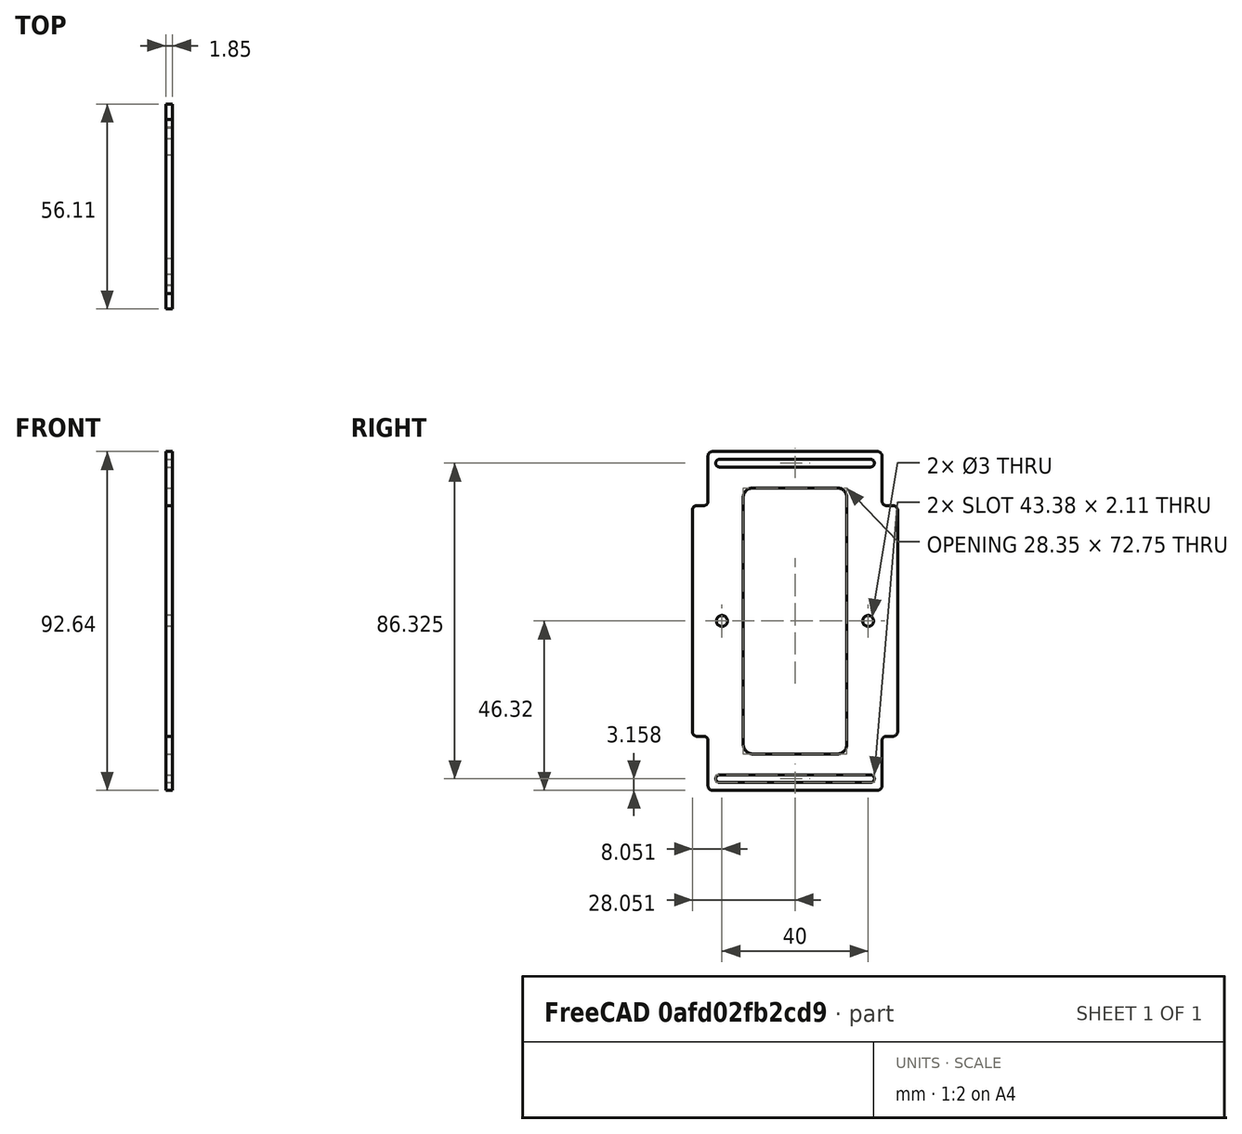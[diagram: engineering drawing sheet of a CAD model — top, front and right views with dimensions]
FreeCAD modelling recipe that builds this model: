
FCSTD DOCUMENT  (FreeCAD 1.0R38641 +468 (Git))
Label: psu_side_short
License: All rights reserved
LicenseURL: https://en.wikipedia.org/wiki/All_rights_reserved
objects: PartDesign::SubShapeBinder×2, Sketcher::SketchObject×1, PartDesign::Pad×1, PartDesign::Body×1
note: 8 computed .brp shape members not serialized (recipe doc carries the construction recipe); baked Part::Feature solids carry a one-line shape summary decoded from their .brp
EXTERNAL_REF file=../../third_party/qualtek_power_entry.FCStd obj=Body
EXTERNAL_REF file=psu_top_and_bottom.FCStd obj=Body
EXTERNAL_REF file=../dimensions.FCStd obj=VarSet

FEATURE [PartDesign::SubShapeBinder] Binder  label="PowerEntryBinder"
  BindCopyOnChange = 0
  BindMode = 0
  ClaimChildren = false
  Context = -> Body [Binder.]
  Fuse = false
  MakeFace = true
  OffsetFill = false
  OffsetIntersection = false
  OffsetJoinType = 0
  OffsetOpenResult = false
  PartialLoad = false
  Placement = pos=(0,0,0) rot=(1,0,0;1.5708rad)
  Refine = true
  Relative = true
  Support = -> [<external ../../third_party/qualtek_power_entry.FCStd>#Body]
  _Version = 2
FEATURE [PartDesign::SubShapeBinder] Binder001  label="PsuTopAndBottomBinder"
  BindCopyOnChange = 0
  BindMode = 0
  ClaimChildren = false
  Context = -> Body [Binder001.]
  Fuse = false
  MakeFace = true
  OffsetFill = false
  OffsetIntersection = false
  OffsetJoinType = 0
  OffsetOpenResult = false
  PartialLoad = false
  Refine = true
  Relative = true
  Support = -> [<external psu_top_and_bottom.FCStd>#Body]
  _Version = 2
FEATURE [Sketcher::SketchObject] Sketch
  ArcFitTolerance = 1e-06
  AttachmentSupport = -> [Binder001]
  ExternalGeometry = -> [Binder001,Binder]
  FullyConstrained = true
  MakeInternals = false
  MapMode = 5
  Placement = pos=(326.108,0,0) rot=(0.57735,0.57735,0.57735;2.0944rad)
  expr: Constraints[141] = dimensions#VarSet.EnclosureFinishThickness
  expr: Constraints[165] = dimensions#VarSet.EnclosureTotalThickness + 2 * dimensions#VarSet.EnclosureFinishThickness
  expr: Constraints[2] = dimensions#VarSet.EnclosureFinishThickness
  expr: Constraints[31] = dimensions#VarSet.EnclosureCornerRadius
  expr: Constraints[3] = dimensions#VarSet.EnclosureFinishThickness
  sketch-geometry (76):
    g0: LineSegment [constr] StartX=129.081 StartY=-24.706 StartZ=0 EndX=129.081 EndY=-87.794 EndZ=0
    g1: LineSegment StartX=129.081 StartY=-24.706 StartZ=0 EndX=127.227 EndY=-24.706 EndZ=0
    g2: LineSegment StartX=129.081 StartY=-87.794 StartZ=0 EndX=127.227 EndY=-87.794 EndZ=0
    g3: LineSegment StartX=126.027 StartY=-86.594 StartZ=0 EndX=126.027 EndY=-25.906 EndZ=0
    g4: ArcOfCircle CenterX=129.081 CenterY=-88.994 CenterZ=0 NormalX=0 NormalY=0 NormalZ=1 AngleXU=0 Radius=1.2 StartAngle=-2.7e-15 EndAngle=1.5708
    g5: ArcOfCircle CenterX=129.081 CenterY=-23.506 CenterZ=0 NormalX=0 NormalY=0 NormalZ=1 AngleXU=0 Radius=1.2 StartAngle=4.71239 EndAngle=6.28319
    g6: LineSegment StartX=130.281 StartY=-11.1254 StartZ=0 EndX=130.281 EndY=-23.506 EndZ=0
    g7: LineSegment StartX=130.281 StartY=-88.994 StartZ=0 EndX=130.281 EndY=-101.375 EndZ=0
    g8: LineSegment StartX=131.481 StartY=-102.575 StartZ=0 EndX=176.681 EndY=-102.575 EndZ=0
    g9: LineSegment StartX=131.481 StartY=-9.9254 StartZ=0 EndX=176.681 EndY=-9.9254 EndZ=0
    g10: LineSegment StartX=177.881 StartY=-11.1254 StartZ=0 EndX=177.881 EndY=-23.506 EndZ=0
    g11: LineSegment StartX=179.081 StartY=-24.706 StartZ=0 EndX=180.935 EndY=-24.706 EndZ=0
    g12: LineSegment StartX=182.135 StartY=-25.906 StartZ=0 EndX=182.135 EndY=-86.594 EndZ=0
    g13: LineSegment StartX=180.935 StartY=-87.794 StartZ=0 EndX=179.081 EndY=-87.794 EndZ=0
    g14: LineSegment StartX=177.881 StartY=-88.994 StartZ=0 EndX=177.881 EndY=-101.375 EndZ=0
    g15: ArcOfCircle CenterX=179.081 CenterY=-23.506 CenterZ=0 NormalX=0 NormalY=0 NormalZ=1 AngleXU=0 Radius=1.2 StartAngle=3.14159 EndAngle=4.71239
    g16: GeomPoint [constr] X=177.881 Y=-24.706 Z=0
    g17: ArcOfCircle CenterX=179.081 CenterY=-88.994 CenterZ=0 NormalX=0 NormalY=0 NormalZ=1 AngleXU=0 Radius=1.2 StartAngle=1.5708 EndAngle=3.14159
    g18: ArcOfCircle CenterX=127.227 CenterY=-25.906 CenterZ=0 NormalX=0 NormalY=0 NormalZ=1 AngleXU=0 Radius=1.2 StartAngle=1.5708 EndAngle=3.14159
    g19: GeomPoint [constr] X=126.027 Y=-24.706 Z=0
    g20: ArcOfCircle CenterX=127.227 CenterY=-86.594 CenterZ=0 NormalX=0 NormalY=0 NormalZ=1 AngleXU=0 Radius=1.2 StartAngle=3.14159 EndAngle=4.71239
    g21: GeomPoint [constr] X=126.027 Y=-87.794 Z=0
    g22: ArcOfCircle CenterX=131.481 CenterY=-101.375 CenterZ=0 NormalX=0 NormalY=0 NormalZ=1 AngleXU=0 Radius=1.2 StartAngle=3.14159 EndAngle=4.71239
    g23: GeomPoint [constr] X=130.281 Y=-102.575 Z=0
    g24: ArcOfCircle CenterX=176.681 CenterY=-101.375 CenterZ=0 NormalX=0 NormalY=0 NormalZ=1 AngleXU=0 Radius=1.2 StartAngle=4.71239 EndAngle=6.28319
    g25: GeomPoint [constr] X=177.881 Y=-102.575 Z=0
    g26: ArcOfCircle CenterX=180.935 CenterY=-86.594 CenterZ=0 NormalX=0 NormalY=0 NormalZ=1 AngleXU=0 Radius=1.2 StartAngle=4.71239 EndAngle=6.28319
    g27: GeomPoint [constr] X=182.135 Y=-87.794 Z=0
    g28: ArcOfCircle CenterX=180.935 CenterY=-25.906 CenterZ=0 NormalX=0 NormalY=0 NormalZ=1 AngleXU=0 Radius=1.2 StartAngle=0 EndAngle=1.5708
    g29: GeomPoint [constr] X=182.135 Y=-24.706 Z=0
    g30: ArcOfCircle CenterX=176.681 CenterY=-11.1254 CenterZ=0 NormalX=0 NormalY=0 NormalZ=1 AngleXU=0 Radius=1.2 StartAngle=0 EndAngle=1.5708
    g31: GeomPoint [constr] X=177.881 Y=-9.9254 Z=0
    g32: ArcOfCircle CenterX=131.481 CenterY=-11.1254 CenterZ=0 NormalX=0 NormalY=0 NormalZ=1 AngleXU=0 Radius=1.2 StartAngle=1.5708 EndAngle=3.14159
    g33: GeomPoint [constr] X=130.281 Y=-9.9254 Z=0
    g34: Circle CenterX=134.081 CenterY=-56.25 CenterZ=0 NormalX=0 NormalY=0 NormalZ=1 AngleXU=0 Radius=1.5
    g35: Circle CenterX=174.081 CenterY=-56.25 CenterZ=0 NormalX=0 NormalY=0 NormalZ=1 AngleXU=0 Radius=1.5
    g36: LineSegment [constr] StartX=140.031 StartY=-22.5 StartZ=0 EndX=140.031 EndY=-90 EndZ=0
    g37: LineSegment [constr] StartX=142.531 StartY=-92.5 StartZ=0 EndX=165.631 EndY=-92.5 EndZ=0
    g38: LineSegment [constr] StartX=168.131 StartY=-90 StartZ=0 EndX=168.131 EndY=-22.5 EndZ=0
    g39: LineSegment [constr] StartX=165.631 StartY=-20 StartZ=0 EndX=142.531 EndY=-20 EndZ=0
    g40: ArcOfCircle [constr] CenterX=142.531 CenterY=-22.5 CenterZ=0 NormalX=0 NormalY=0 NormalZ=1 AngleXU=0 Radius=2.5 StartAngle=1.5708 EndAngle=3.14159
    g41: ArcOfCircle [constr] CenterX=142.531 CenterY=-90 CenterZ=0 NormalX=0 NormalY=0 NormalZ=1 AngleXU=0 Radius=2.5 StartAngle=3.14159 EndAngle=4.71239
    g42: ArcOfCircle [constr] CenterX=165.631 CenterY=-90 CenterZ=0 NormalX=0 NormalY=0 NormalZ=1 AngleXU=0 Radius=2.5 StartAngle=4.71239 EndAngle=6.28319
    g43: ArcOfCircle [constr] CenterX=165.631 CenterY=-22.5 CenterZ=0 NormalX=0 NormalY=0 NormalZ=1 AngleXU=0 Radius=2.5 StartAngle=5e-16 EndAngle=1.5708
    g44: GeomPoint [constr] X=140.031 Y=-20 Z=0
    g45: GeomPoint [constr] X=168.131 Y=-92.5 Z=0
    g46: LineSegment [constr] StartX=126.027 StartY=-56.25 StartZ=0 EndX=134.081 EndY=-56.25 EndZ=0
    g47: LineSegment [constr] StartX=134.081 StartY=-56.25 StartZ=0 EndX=140.031 EndY=-56.25 EndZ=0
    g48: LineSegment [constr] StartX=168.131 StartY=-56.25 StartZ=0 EndX=174.081 EndY=-56.25 EndZ=0
    g49: LineSegment [constr] StartX=174.081 StartY=-56.25 StartZ=0 EndX=182.135 EndY=-56.25 EndZ=0
    g50: LineSegment [constr] StartX=-45 StartY=1.4e-14 StartZ=0 EndX=-39.05 EndY=1.31e-14 EndZ=0
    g51: LineSegment [constr] StartX=-10.95 StartY=6.1e-15 StartZ=0 EndX=-5 EndY=-1.07e-14 EndZ=0
    g52: LineSegment StartX=139.904 StartY=-22.5 StartZ=0 EndX=139.904 EndY=-90 EndZ=0
    g53: LineSegment StartX=142.531 StartY=-92.627 StartZ=0 EndX=165.631 EndY=-92.627 EndZ=0
    g54: LineSegment StartX=168.258 StartY=-90 StartZ=0 EndX=168.258 EndY=-22.5 EndZ=0
    g55: LineSegment StartX=165.631 StartY=-19.873 StartZ=0 EndX=142.531 EndY=-19.873 EndZ=0
    g56: ArcOfCircle CenterX=142.531 CenterY=-22.5 CenterZ=0 NormalX=0 NormalY=0 NormalZ=1 AngleXU=0 Radius=2.627 StartAngle=1.5708 EndAngle=3.14159
    g57: ArcOfCircle CenterX=142.531 CenterY=-90 CenterZ=0 NormalX=0 NormalY=0 NormalZ=1 AngleXU=0 Radius=2.627 StartAngle=3.14159 EndAngle=4.71239
    g58: ArcOfCircle CenterX=165.631 CenterY=-90 CenterZ=0 NormalX=0 NormalY=0 NormalZ=1 AngleXU=0 Radius=2.627 StartAngle=4.71239 EndAngle=6.28319
    g59: ArcOfCircle CenterX=165.631 CenterY=-22.5 CenterZ=0 NormalX=0 NormalY=0 NormalZ=1 AngleXU=0 Radius=2.627 StartAngle=5e-16 EndAngle=1.5708
    g60: GeomPoint [constr] X=139.904 Y=-19.873 Z=0
    g61: GeomPoint [constr] X=168.258 Y=-92.627 Z=0
    g62: LineSegment [constr] StartX=-50 StartY=7.1e-15 StartZ=0 EndX=0 EndY=0 EndZ=0
    g63: LineSegment [constr] StartX=129.081 StartY=-87.794 StartZ=0 EndX=179.081 EndY=-87.794 EndZ=0
    g64: ArcOfCircle CenterX=133.444 CenterY=-13.0877 CenterZ=0 NormalX=0 NormalY=0 NormalZ=1 AngleXU=0 Radius=1.0541 StartAngle=1.5708 EndAngle=4.71239
    g65: ArcOfCircle CenterX=174.719 CenterY=-13.0877 CenterZ=0 NormalX=0 NormalY=0 NormalZ=1 AngleXU=0 Radius=1.0541 StartAngle=4.71239 EndAngle=7.85398
    g66: LineSegment StartX=133.444 StartY=-12.0336 StartZ=0 EndX=174.719 EndY=-12.0336 EndZ=0
    g67: LineSegment StartX=133.444 StartY=-14.1418 StartZ=0 EndX=174.719 EndY=-14.1418 EndZ=0
    g68: ArcOfCircle CenterX=133.444 CenterY=-99.4123 CenterZ=0 NormalX=0 NormalY=0 NormalZ=1 AngleXU=0 Radius=1.0541 StartAngle=1.5708 EndAngle=4.71239
    g69: ArcOfCircle CenterX=174.719 CenterY=-99.4123 CenterZ=0 NormalX=0 NormalY=0 NormalZ=1 AngleXU=0 Radius=1.0541 StartAngle=4.71239 EndAngle=7.85398
    g70: LineSegment StartX=133.444 StartY=-98.3582 StartZ=0 EndX=174.719 EndY=-98.3582 EndZ=0
    g71: LineSegment StartX=133.444 StartY=-100.466 StartZ=0 EndX=174.719 EndY=-100.466 EndZ=0
    g72: LineSegment [constr] StartX=154.081 StartY=-102.575 StartZ=0 EndX=154.081 EndY=-100.466 EndZ=0
    g73: LineSegment [constr] StartX=154.081 StartY=-9.9254 StartZ=0 EndX=154.081 EndY=-12.0336 EndZ=0
    g74: LineSegment [constr] StartX=154.081 StartY=-98.3582 StartZ=0 EndX=154.081 EndY=-100.466 EndZ=0
    g75: LineSegment [constr] StartX=130.281 StartY=-99.4123 StartZ=0 EndX=132.389 EndY=-99.4123 EndZ=0
  constraints (177):
    c: PointOnObject(g0,g-3)
    c: PointOnObject(g0,g-3)
    c: DistanceY(g-3,g0) = 0.127
    c: DistanceY(g0,g-3) = 0.127
    c: Horizontal(g1)
    c: Horizontal(g2)
    c: Vertical(g3)
    c: Vertical(g6)
    c: Tangent(g5,g6) = 1.5708
    c: Vertical(g7)
    c: Tangent(g7,g4) = 1.5708
    c: Horizontal(g8)
    c: Horizontal(g9)
    c: Vertical(g10)
    c: Horizontal(g11)
    c: Vertical(g12)
    c: Horizontal(g13)
    c: Vertical(g14)
    c: PointOnObject(g16,g10)
    c: PointOnObject(g16,g11)
    c: Tangent(g10,g15) = -1.5708
    c: Tangent(g11,g15) = -1.5708
    c: Tangent(g2,g4) = -1.5708
    c: Coincident(g0,g2)
    c: Tangent(g14,g17) = -1.5708
    c: Tangent(g17,g13) = -1.5708
    c: Equal(g17,g4)
    c: Equal(g4,g5)
    c: Tangent(g1,g5) = 1.5708
    c: Coincident(g1,g0)
    c: Equal(g17,g15)
    c: Radius(g4) = 1.2
    c: PointOnObject(g19,g1)
    c: PointOnObject(g19,g3)
    c: Tangent(g1,g18) = -1.5708
    c: Tangent(g3,g18) = 1.5708
    c: PointOnObject(g21,g2)
    c: PointOnObject(g21,g3)
    c: Tangent(g2,g20) = 1.5708
    c: Tangent(g3,g20) = 1.5708
    c: PointOnObject(g23,g7)
    c: PointOnObject(g23,g8)
    c: Tangent(g7,g22) = -1.5708
    c: Tangent(g8,g22) = -1.5708
    c: PointOnObject(g25,g8)
    c: PointOnObject(g25,g14)
    c: Tangent(g8,g24) = -1.5708
    c: Tangent(g14,g24) = 1.5708
    c: PointOnObject(g27,g12)
    c: PointOnObject(g27,g13)
    c: Tangent(g12,g26) = 1.5708
    c: Tangent(g13,g26) = 1.5708
    c: PointOnObject(g29,g11)
    c: PointOnObject(g29,g12)
    c: Tangent(g11,g28) = 1.5708
    c: Tangent(g12,g28) = 1.5708
    c: PointOnObject(g31,g9)
    c: PointOnObject(g31,g10)
    c: Tangent(g9,g30) = 1.5708
    c: Tangent(g10,g30) = 1.5708
    c: PointOnObject(g33,g6)
    c: PointOnObject(g33,g9)
    c: Tangent(g6,g32) = -1.5708
    c: Tangent(g9,g32) = 1.5708
    c: PointOnObject(g-4,g9)
    c: Equal(g32,g5)
    c: Equal(g5,g18)
    c: Equal(g18,g20)
    c: Equal(g4,g22)
    c: Equal(g22,g24)
    c: Equal(g17,g26)
    c: Equal(g26,g28)
    c: Equal(g30,g15)
    c: Equal(g11,g13)
    c: Equal(g14,g10)
    c: Equal(g13,g2)
    c: Equal(g6,g10)
    c: Equal(g14,g7)
    c: PointOnObject(g2,g-5)
    c: Tangent(g36,g40) = -1.5708
    c: Tangent(g36,g41) = -1.5708
    c: Tangent(g37,g41) = -1.5708
    c: Tangent(g37,g42) = -1.5708
    c: Tangent(g38,g42) = -1.5708
    c: Tangent(g38,g43) = -1.5708
    c: Tangent(g39,g43) = -1.5708
    c: Tangent(g39,g40) = -1.5708
    c: Vertical(g36)
    c: Vertical(g38)
    c: Horizontal(g37)
    c: Horizontal(g39)
    c: Equal(g40,g41)
    c: Equal(g41,g42)
    c: Equal(g42,g43)
    c: PointOnObject(g44,g36)
    c: PointOnObject(g44,g39)
    c: PointOnObject(g45,g37)
    c: PointOnObject(g45,g38)
    c: Equal(g40,g-15)
    c: Equal(g39,g-14)
    c: Equal(g36,g-8)
    c: Symmetric(g3,g3,g46)
    c: Coincident(g46,g34)
    c: Horizontal(g46)
    c: Coincident(g47,g34)
    c: Symmetric(g36,g36,g47)
    c: Horizontal(g47)
    c: Symmetric(g38,g38,g48)
    c: Coincident(g48,g35)
    c: Horizontal(g48)
    c: Equal(g46,g49)
    c: Coincident(g50,g-7)
    c: Symmetric(g-8,g-8,g50)
    c: Symmetric(g-12,g-12,g51)
    c: Coincident(g51,g-6)
    c: Equal(g51,g48)
    c: Equal(g47,g50)
    c: Coincident(g49,g35)
    c: Symmetric(g12,g12,g49)
    c: Diameter(g34) = 3
    c: Equal(g35,g34)
    c: Tangent(g52,g56) = -1.5708
    c: Tangent(g52,g57) = -1.5708
    c: Tangent(g53,g57) = -1.5708
    c: Tangent(g53,g58) = -1.5708
    c: Tangent(g54,g58) = -1.5708
    c: Tangent(g54,g59) = -1.5708
    c: Tangent(g55,g59) = -1.5708
    c: Tangent(g55,g56) = -1.5708
    c: Vertical(g52)
    c: Vertical(g54)
    c: Horizontal(g53)
    c: Horizontal(g55)
    c: Equal(g58,g59)
    c: PointOnObject(g60,g52)
    c: PointOnObject(g60,g55)
    c: PointOnObject(g61,g53)
    c: PointOnObject(g61,g54)
    c: Coincident(g58,g42)
    c: Coincident(g57,g41)
    c: Coincident(g56,g40)
    c: Distance(g55,g39) = 0.127
    c: Coincident(g62,g-16)
    c: Coincident(g62,g-1)
    c: Coincident(g63,g0)
    c: Coincident(g63,g13)
    c: Equal(g63,g62)
    c: Tangent(g64,g66) = 1.5708
    c: Tangent(g64,g67) = -1.5708
    c: Tangent(g65,g66) = 1.5708
    c: Tangent(g65,g67) = -1.5708
    c: Equal(g64,g65)
    c: Horizontal(g66)
    c: Tangent(g68,g70) = 1.5708
    c: Tangent(g68,g71) = -1.5708
    c: Tangent(g69,g70) = 1.5708
    c: Tangent(g69,g71) = -1.5708
    c: Equal(g68,g69)
    c: Horizontal(g70)
    c: Symmetric(g8,g8,g72)
    c: Symmetric(g71,g71,g72)
    c: Vertical(g72)
    c: Symmetric(g9,g9,g73)
    c: Symmetric(g66,g66,g73)
    c: Vertical(g73)
    c: Distance(g71,g70) = 2.1082
    c: Equal(g72,g73)
    c: Symmetric(g70,g70,g74)
    c: Coincident(g74,g72)
    c: Equal(g74,g72)
    c: PointOnObject(g75,g7)
    c: PointOnObject(g75,g68)
    c: Horizontal(g75)
    c: Equal(g75,g72)
    c: Equal(g64,g68)
    c: Equal(g67,g70)
    c: Perpendicular(g68,g75)
FEATURE [PartDesign::Pad] Pad
  Direction = (1,0,0)
  Length = 1.8542
  Length2 = 10
  Profile = -> Sketch
  ReferenceAxis = -> Sketch [N_Axis]
  Refine = true
  Suppressed = false
  Type = 0
  expr: Length = dimensions#VarSet.EnclosureTotalThickness
FEATURE [PartDesign::Body] Body  label="PsuSideShort"
  AllowCompound = false
  Group = -> [Binder,Binder001,Sketch,Pad]
  Origin = -> Origin
  Tip = -> Pad
